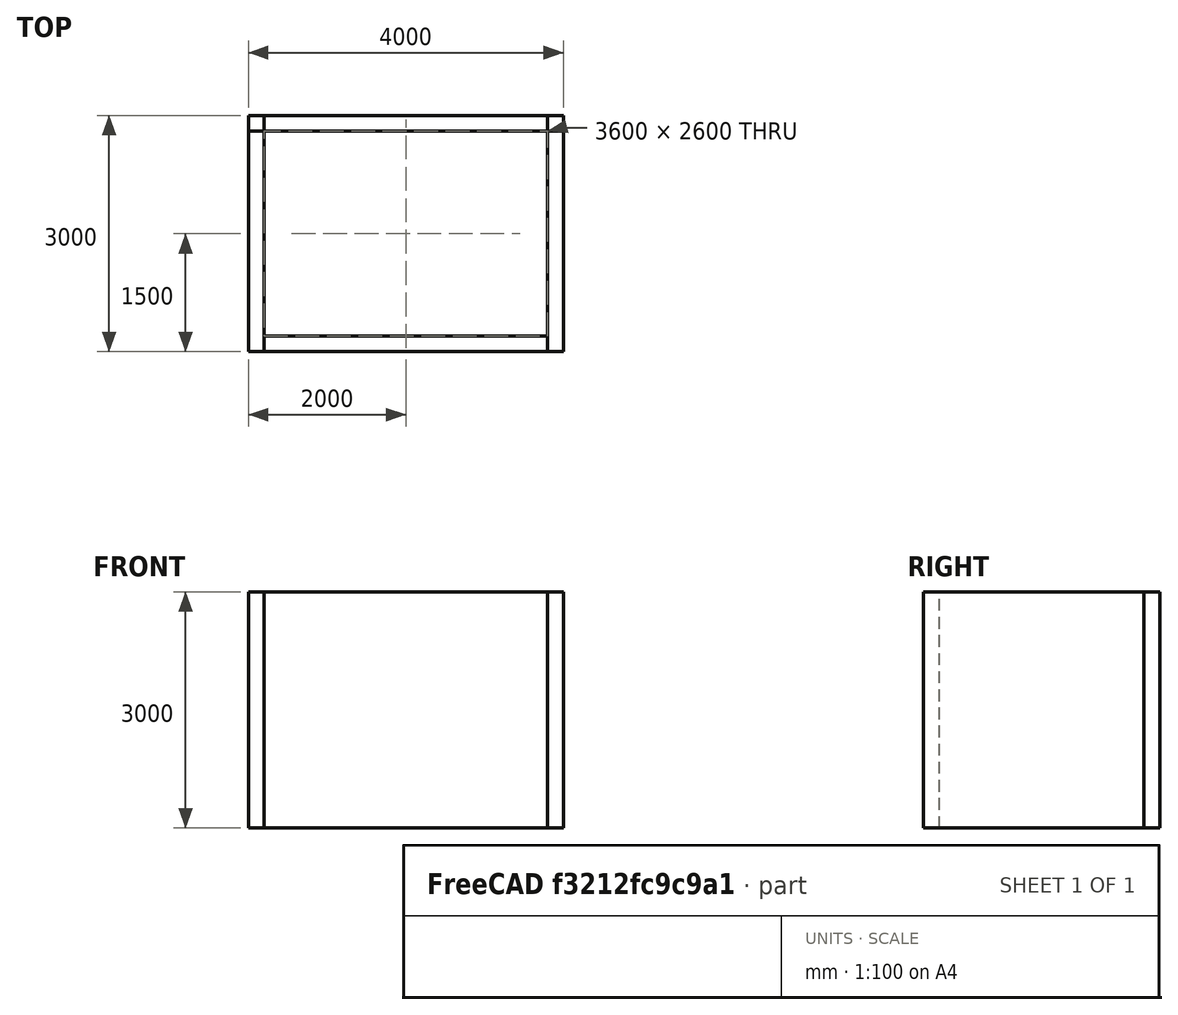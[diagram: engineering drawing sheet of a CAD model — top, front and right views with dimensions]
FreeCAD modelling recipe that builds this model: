
FCSTD DOCUMENT  (FreeCAD 0.19RUnknown)
Label: bim2
License: All rights reserved
LicenseURL: http://en.wikipedia.org/wiki/All_rights_reserved
objects: Part::Part2DObjectPython×4, Part::FeaturePython×4
note: 8 computed .brp shape members not serialized (recipe doc carries the construction recipe); baked Part::Feature solids carry a one-line shape summary decoded from their .brp

FEATURE [Part::Part2DObjectPython] Line  # Draft 2D object (typed FeaturePython)
  Area = 0
  ChamferSize = 0
  Closed = false
  End = (0,3000,0)
  FilletRadius = 0
  Length = 3000
  MakeFace = true
  Points = (2) [(0,0,0),(9.18485e-14,3000,0)]
  Start = (0,0,0)
  Subdivisions = 0
FEATURE [Part::Part2DObjectPython] Line001  # Draft 2D object (typed FeaturePython)
  Area = 0
  ChamferSize = 0
  Closed = false
  End = (4000,3000,0)
  FilletRadius = 0
  Length = 4000
  MakeFace = true
  Placement = pos=(0,3000,0) rot=(0,0,1;0rad)
  Points = (2) [(0,0,0),(4000,4.54747e-13,0)]
  Start = (0,3000,0)
  Subdivisions = 0
FEATURE [Part::Part2DObjectPython] Line002  # Draft 2D object (typed FeaturePython)
  Area = 0
  ChamferSize = 0
  Closed = false
  End = (4000,0,0)
  FilletRadius = 0
  Length = 3000
  MakeFace = true
  Placement = pos=(4000,3000,0) rot=(0,0,1;0rad)
  Points = (2) [(0,0,0),(0,-3000,0)]
  Start = (4000,3000,0)
  Subdivisions = 0
FEATURE [Part::Part2DObjectPython] Line003  # Draft 2D object (typed FeaturePython)
  Area = 0
  ChamferSize = 0
  Closed = false
  End = (0,0,0)
  FilletRadius = 0
  Length = 4000
  MakeFace = true
  Placement = pos=(4000,0,0) rot=(0,0,1;0rad)
  Points = (2) [(0,0,0),(-4000,1.22465e-13,0)]
  Start = (4000,0,0)
  Subdivisions = 0
FEATURE [Part::FeaturePython] Wall  # Arch/BIM 166 (typed FeaturePython)
  Align = 0
  Area = 9000000
  Base = -> Line
  BlockHeight = 0
  BlockLength = 0
  CountBroken = 0
  CountEntire = 0
  Face = 0
  Height = 3000
  HorizontalArea = 600000
  IfcData = attributes={"GlobalId": {"name": "GlobalId", "type": "IfcGloballyUniqueId", "is_enum": false, "enum_values": []}, "Description": {"... (+533 chars omitted),+1 more (map truncated)
  IfcType = 166
  Joint = 0
  Length = 3000
  MakeBlocks = false
  MoveBase = false
  MoveWithHost = false
  Normal = (0,0,0)
  OffsetFirst = 0
  OffsetSecond = 0
  PerimeterLength = 6400
  PredefinedType = 0
  VerticalArea = 19200000
  Width = 200
FEATURE [Part::FeaturePython] Wall001  # Arch/BIM 166 (typed FeaturePython)
  Align = 0
  Area = 12000000
  Base = -> Line001
  BlockHeight = 0
  BlockLength = 0
  CountBroken = 0
  CountEntire = 0
  Face = 0
  Height = 3000
  HorizontalArea = 800000
  IfcData = attributes={"GlobalId": {"name": "GlobalId", "type": "IfcGloballyUniqueId", "is_enum": false, "enum_values": []}, "Description": {"... (+533 chars omitted),+1 more (map truncated)
  IfcType = 166
  Joint = 0
  Length = 4000
  MakeBlocks = false
  MoveBase = false
  MoveWithHost = false
  Normal = (0,0,0)
  OffsetFirst = 0
  OffsetSecond = 0
  PerimeterLength = 8400
  PredefinedType = 0
  VerticalArea = 2.52e+07
  Width = 200
FEATURE [Part::FeaturePython] Wall002  # Arch/BIM 166 (typed FeaturePython)
  Align = 0
  Area = 9000000
  Base = -> Line002
  BlockHeight = 0
  BlockLength = 0
  CountBroken = 0
  CountEntire = 0
  Face = 0
  Height = 3000
  HorizontalArea = 600000
  IfcData = attributes={"GlobalId": {"name": "GlobalId", "type": "IfcGloballyUniqueId", "is_enum": false, "enum_values": []}, "Description": {"... (+533 chars omitted),+1 more (map truncated)
  IfcType = 166
  Joint = 0
  Length = 3000
  MakeBlocks = false
  MoveBase = false
  MoveWithHost = false
  Normal = (0,0,0)
  OffsetFirst = 0
  OffsetSecond = 0
  PerimeterLength = 6400
  PredefinedType = 0
  VerticalArea = 19200000
  Width = 200
FEATURE [Part::FeaturePython] Wall003  # Arch/BIM 166 (typed FeaturePython)
  Additions = -> [Wall,Wall001,Wall002]
  Align = 0
  Area = 12000000
  Base = -> Line003
  BlockHeight = 0
  BlockLength = 0
  CountBroken = 0
  CountEntire = 0
  Face = 0
  Height = 3000
  HorizontalArea = 2.64e+06
  IfcData = attributes={"GlobalId": {"name": "GlobalId", "type": "IfcGloballyUniqueId", "is_enum": false, "enum_values": []}, "Description": {"... (+533 chars omitted),+1 more (map truncated)
  IfcType = 166
  Joint = 0
  Length = 4000
  MakeBlocks = false
  MoveBase = false
  MoveWithHost = false
  Normal = (0,0,0)
  OffsetFirst = 0
  OffsetSecond = 0
  PerimeterLength = 14000
  PredefinedType = 0
  VerticalArea = 79200000
  Width = 200
